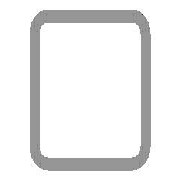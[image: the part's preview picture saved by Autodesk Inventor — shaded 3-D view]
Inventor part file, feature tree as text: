
AUTODESK INVENTOR PART (.ipt)
format: ipt  version: 2022 (Build 260153000, 153)  size: 265,728 bytes
history: native  units: mm (DEFAULTED — no unit token found)
features: other x7, sketch x3, surface_op x2, plane x1
ambient origin geometry x8: Origin, YZ Plane, XZ Plane, XY Plane, X Axis, Y Axis, Z Axis, Center Point
bodies: Body (feature_tree), Solid6 (feature_tree)
feature tree (13):
  parser-record x1  (decoder bookkeeping rows leaked as tree rows — omitted from the tree; the rows remain in map.json)
  other  "Driven Length"
  other  "Start Plane"
  other  "End Plane"
  sketch  "Sketch"  dims[d7=8.0mm d9=40.0mm d11=40.0mm d12=4.0mm d13=-0.0mm d14=180.0mm d15=20.0mm d16=20.0mm d17=90.0deg d18=180.0mm d91=5.0mm d92=5.0mm d93=5.0mm d94=5.0mm d95=5.0mm d96=5.0mm d97=5.0mm d98=5.0mm d99=0.0mm d100=5.0mm d101=5.0mm d102=5.0mm d103=5.0mm d104=5.0mm d105=5.0mm d106=5.0mm d107=5.0mm d108=0.0mm]
  sketch  "Sketch3"  dims[d3=155.0mm]
  plane  "Work Plane3"
  sketch  "Sketch4"  dims[d4=0.0mm]
  other  "Srf14"
  other  "Srf15"
  other  "Srf13"
  surface_op  "Boundary Patch9"
  surface_op  "Boundary Patch10"
